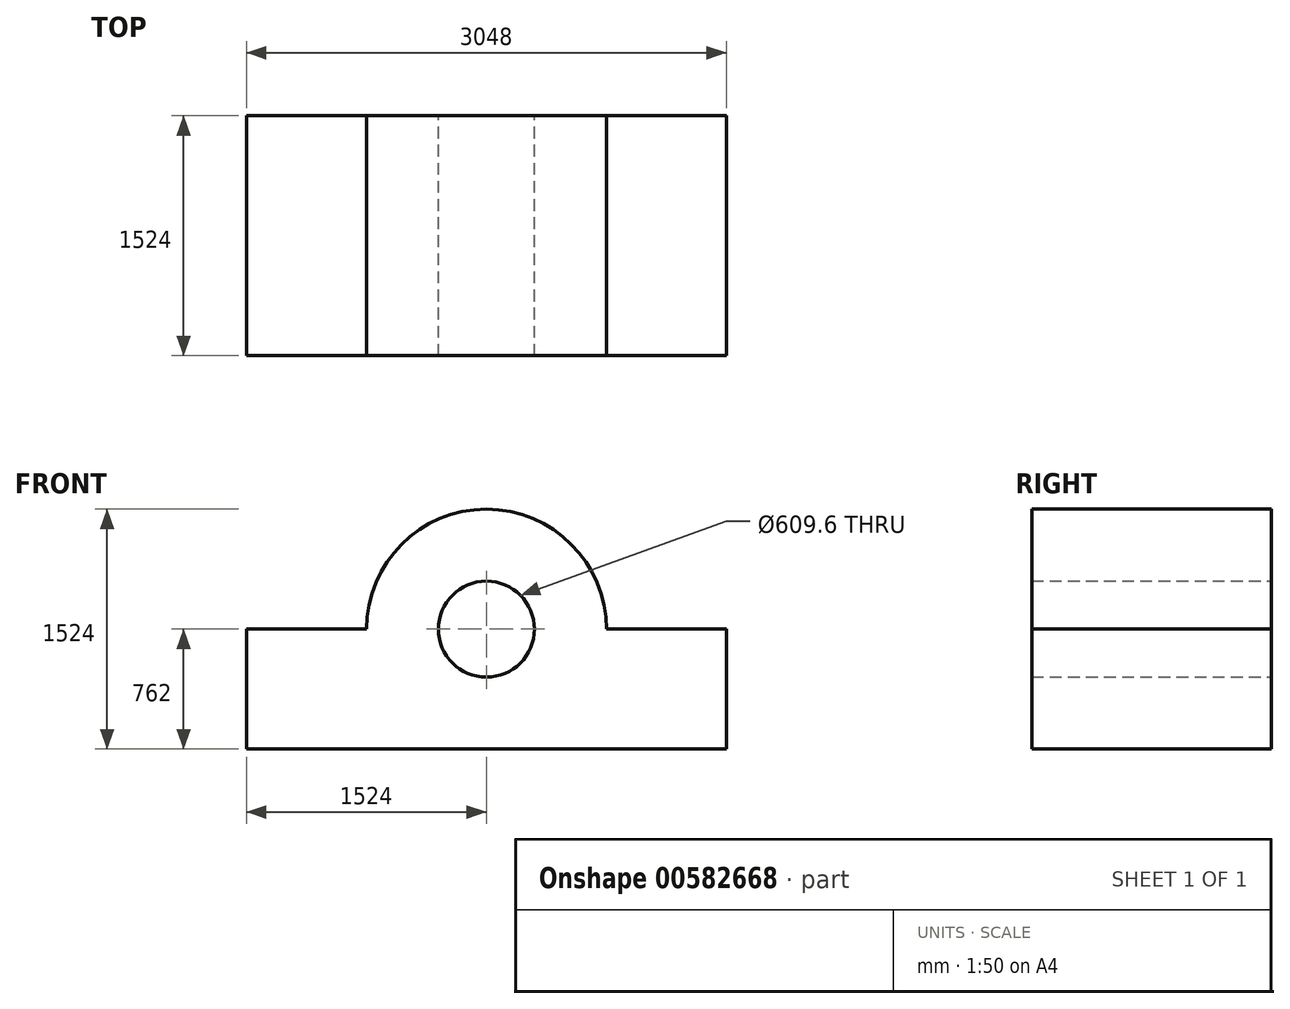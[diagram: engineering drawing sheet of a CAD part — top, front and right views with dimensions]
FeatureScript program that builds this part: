
annotation { "Feature Type Name" : "Feature", "Feature Type Description" : "" }
export const myFeature = defineFeature(function(context is Context, id is Id, definition is map)
    precondition{}
    {
        {
            var Q0;
            Q0=qCreatedBy(makeId("Front.planeOp"),FACE);
            var sketch = newSketch(context, id + "F0", { "sketchPlane" : qUnion([Q0])});
            skCircle(sketch, "E0", {"center": v(0, 0) * mm, "radius": 304.8 * mm});
            skArc(sketch, "E1", {"start": v(762, 0) * mm, "mid": v(0, 762) * mm, "end": v(-762, 0) * mm});
            skLineSegment(sketch, "E2", {"start": v(-762, 0) * mm, "end": v(-1524, 0) * mm});
            skLineSegment(sketch, "E3", {"start": v(762, 0) * mm, "end": v(1524, 0) * mm});
            skLineSegment(sketch, "E4", {"start": v(-1524, 0) * mm, "end": v(-1524, -762) * mm});
            skLineSegment(sketch, "E5", {"start": v(-1524, -762) * mm, "end": v(1524, -762) * mm});
            skLineSegment(sketch, "E6", {"start": v(1524, -762) * mm, "end": v(1524, 0) * mm});
            skSolve(sketch);
        }
        {
            var Q0;
            Q0 = qSketchRegion(id + "F0", true);
            extrude(context, id + "F1", {"entities" : qUnion([Q0]), "depth" : 1524 * mm, "offsetDistance" : 25.4 * mm, "symmetric" : true});
        }
    });
